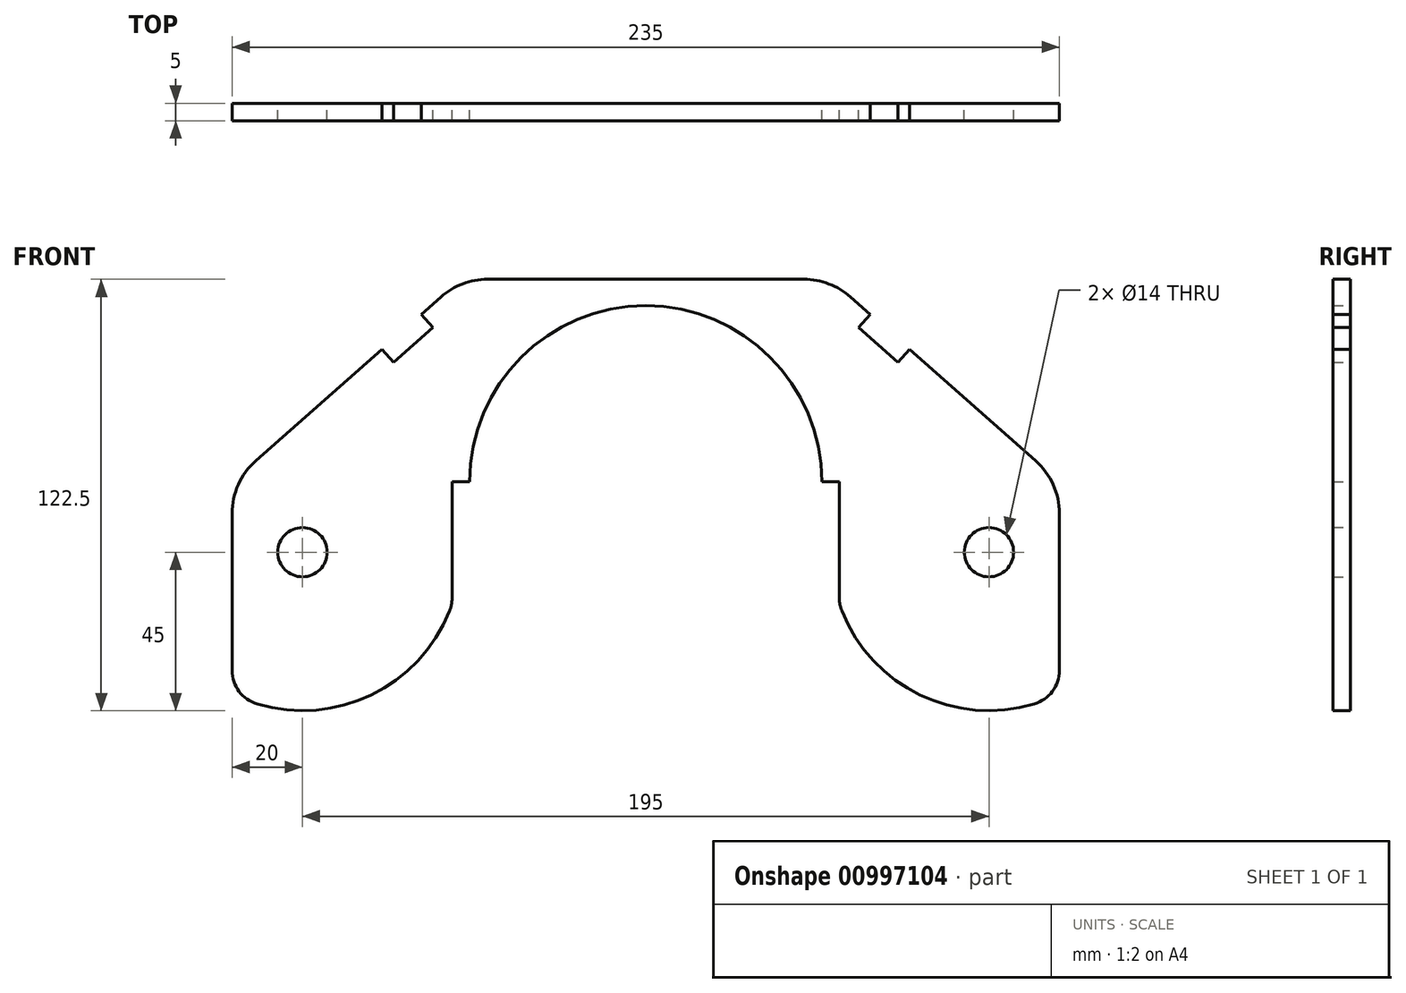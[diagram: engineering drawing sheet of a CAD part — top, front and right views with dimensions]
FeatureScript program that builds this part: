
annotation { "Feature Type Name" : "Feature", "Feature Type Description" : "" }
export const myFeature = defineFeature(function(context is Context, id is Id, definition is map)
    precondition{}
    {
        {
            var Q0;
            Q0=qCreatedBy(makeId("Front.planeOp"),FACE);
            var sketch = newSketch(context, id + "F0", { "sketchPlane" : qUnion([Q0])});
            skArc(sketch, "E0", {"start": v(50, 0) * mm, "mid": v(0, 50) * mm, "end": v(-50, 0) * mm});
            skCircle(sketch, "E1", {"center": v(-97.5, -20) * mm, "radius": 7 * mm});
            skCircle(sketch, "E2", {"center": v(97.5, -20) * mm, "radius": 7 * mm});
            skLineSegment(sketch, "E3", {"start": v(-55, 0) * mm, "end": v(-55, -33) * mm});
            skLineSegment(sketch, "E4", {"start": v(55, 0) * mm, "end": v(55, -33) * mm});
            skLineSegment(sketch, "E5", {"start": v(-55, 0) * mm, "end": v(-50, 0) * mm});
            skLineSegment(sketch, "E6", {"start": v(50, 0) * mm, "end": v(55, 0) * mm});
            skPoint(sketch, "E7.visualSharp", {"position": v(-55, -34.8) * mm});
            skLineSegment(sketch, "E8", {"start": v(-117.5, -53.54) * mm, "end": v(-117.5, -9.01) * mm});
            skLineSegment(sketch, "E9", {"start": v(117.5, -9.01) * mm, "end": v(117.5, -53.54) * mm});
            skArc(sketch, "E10", {"start": v(55.71, -36.7) * mm, "mid": v(77.91, -60.51) * mm, "end": v(110.36, -63.12) * mm});
            skLineSegment(sketch, "E11", {"start": v(-42.5, 57.5) * mm, "end": v(42.5, 57.5) * mm});
            skArc(sketch, "E12.trimOffspring", {"start": v(-110.36, -63.12) * mm, "mid": v(-77.91, -60.51) * mm, "end": v(-55.71, -36.7) * mm});
            skPoint(sketch, "E13", {"position": v(0, 57.5) * mm});
            skPoint(sketch, "E14.visualSharp", {"position": v(117.5, -60.31) * mm});
            skArc(sketch, "E14.filletArc", {"start": v(110.36, -63.12) * mm, "mid": v(115.52, -59.52) * mm, "end": v(117.5, -53.54) * mm});
            skPoint(sketch, "E15.visualSharp", {"position": v(55, -34.8) * mm});
            skArc(sketch, "E15.filletArc", {"start": v(55, -33) * mm, "mid": v(55.18, -34.88) * mm, "end": v(55.71, -36.7) * mm});
            skArc(sketch, "E16.filletArc", {"start": v(-55.71, -36.7) * mm, "mid": v(-55.18, -34.88) * mm, "end": v(-55, -33) * mm});
            skPoint(sketch, "E17.visualSharp", {"position": v(-117.5, -60.31) * mm});
            skArc(sketch, "E17.filletArc", {"start": v(-117.5, -53.54) * mm, "mid": v(-115.52, -59.52) * mm, "end": v(-110.36, -63.12) * mm});
            skLineSegment(sketch, "E18", {"start": v(58.17, 52.48) * mm, "end": v(63.73, 47.56) * mm});
            skPoint(sketch, "E19.visualSharp", {"position": v(117.5, 0) * mm});
            skArc(sketch, "E19.filletArc", {"start": v(117.5, -9.01) * mm, "mid": v(115.73, -0.8) * mm, "end": v(110.75, 5.97) * mm});
            skLineSegment(sketch, "E20.MirrorCS", {"start": v(-58.17, 52.48) * mm, "end": v(-63.73, 47.56) * mm});
            skPoint(sketch, "E21.MirrorP", {"position": v(-117.5, 0) * mm});
            skArc(sketch, "E22.MirrorCS", {"start": v(-117.5, -9.01) * mm, "mid": v(-115.73, -0.8) * mm, "end": v(-110.75, 5.97) * mm});
            skLineSegment(sketch, "E23", {"start": v(-42.5, 57.5) * mm, "end": v(-44.92, 57.5) * mm});
            skLineSegment(sketch, "E24", {"start": v(42.5, 57.5) * mm, "end": v(44.92, 57.5) * mm});
            skPoint(sketch, "E25.visualSharp", {"position": v(-52.5, 57.5) * mm});
            skArc(sketch, "E25.filletArc", {"start": v(-44.92, 57.5) * mm, "mid": v(-52, 56.2) * mm, "end": v(-58.17, 52.48) * mm});
            skPoint(sketch, "E26.visualSharp", {"position": v(52.5, 57.5) * mm});
            skArc(sketch, "E26.filletArc", {"start": v(58.17, 52.48) * mm, "mid": v(52, 56.2) * mm, "end": v(44.92, 57.5) * mm});
            skLineSegment(sketch, "E27", {"start": v(-74.97, 37.62) * mm, "end": v(-71.66, 33.88) * mm});
            skLineSegment(sketch, "E28", {"start": v(-71.66, 33.88) * mm, "end": v(-60.42, 43.82) * mm});
            skLineSegment(sketch, "E29", {"start": v(-60.42, 43.82) * mm, "end": v(-63.73, 47.56) * mm});
            skLineSegment(sketch, "E30.trimOffspring", {"start": v(-74.97, 37.62) * mm, "end": v(-110.75, 5.97) * mm});
            skLineSegment(sketch, "E31.MirrorCS", {"start": v(60.42, 43.82) * mm, "end": v(63.73, 47.56) * mm});
            skLineSegment(sketch, "E32.MirrorCS", {"start": v(71.66, 33.88) * mm, "end": v(60.42, 43.82) * mm});
            skLineSegment(sketch, "E33.MirrorCS", {"start": v(74.97, 37.62) * mm, "end": v(71.66, 33.88) * mm});
            skLineSegment(sketch, "E34.trimOffspring", {"start": v(74.97, 37.62) * mm, "end": v(110.75, 5.97) * mm});
            skSolve(sketch);
        }
        {
            var Q0;
            Q0=qSketchRegion(id+"F0",true);
            extrude(context, id + "F1", {"entities" : qUnion([Q0]), "depth" : 5 * mm, "offsetDistance" : 25 * mm});
        }
    });
